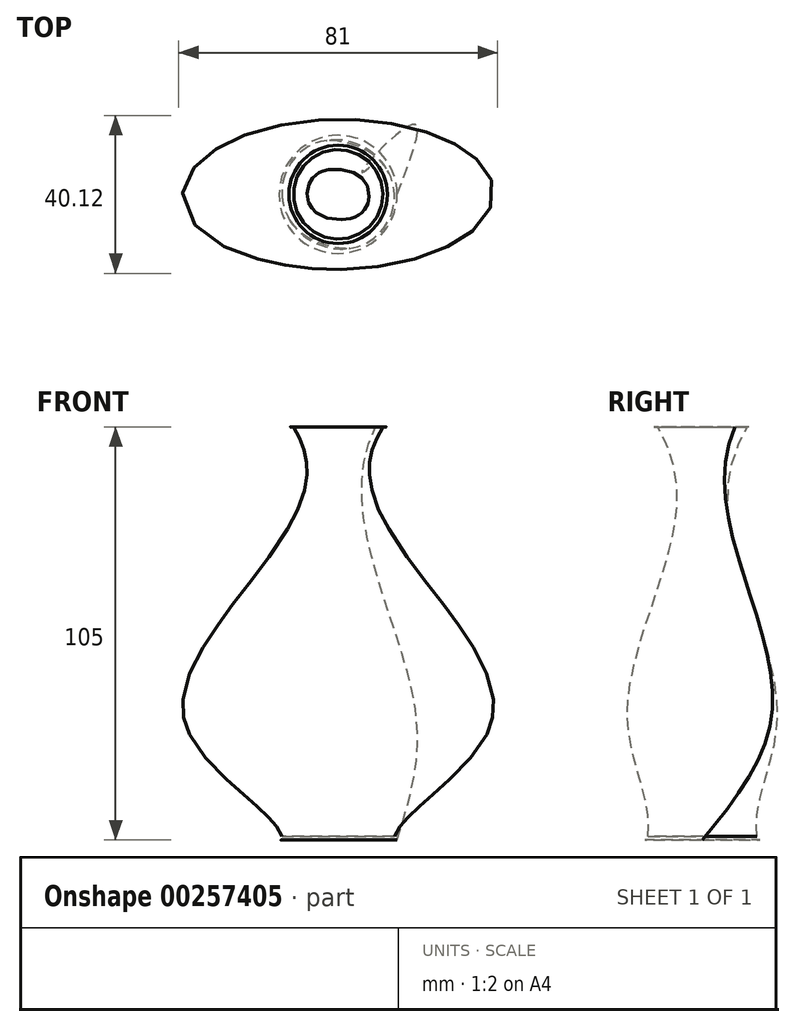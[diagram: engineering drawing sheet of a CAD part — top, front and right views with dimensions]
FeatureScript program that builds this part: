
annotation { "Feature Type Name" : "Feature", "Feature Type Description" : "" }
export const myFeature = defineFeature(function(context is Context, id is Id, definition is map)
    precondition{}
    {
        {
            var Q0;
            Q0=qCreatedBy(makeId("Top.planeOp"),FACE);
            var sketch = newSketch(context, id + "F0", { "sketchPlane" : qUnion([Q0])});
            skCircle(sketch, "E0", {"center": v(0, 0) * mm, "radius": 15 * mm});
            skSolve(sketch);
        }
        {
            var Q0;
            Q0=makeQuery(id+"F0.imprint","IMPRINT",FACE,{"disambiguationData":[TD([[makeQuery(id+"F0.imprint","IMPRINT",EDGE,{"derivedFrom":sQuery(id+"F0.wireOp",EDGE,"E0")}),1.0]])]});
            cPlane(context, id + "F1", {"entities" : qUnion([Q0]), "cplaneType" : CPlaneType.OFFSET, "offset" : 30 * mm, "width" : 150 * mm, "height" : 150 * mm});
        }
        {
            var Q0;
            Q0=qCreatedBy(id+"F1.planeOp",FACE);
            var sketch = newSketch(context, id + "F2", { "sketchPlane" : qUnion([Q0])});
            skEllipse(sketch, "E1", {"center": v(0, 0) * mm, "majorRadius": 40 * mm, "minorRadius": 20 * mm, "majorAxis": v(-1, 0)});
            skSolve(sketch);
        }
        {
            var Q0;
            Q0=makeQuery(id+"F2.imprint","IMPRINT",FACE,{"disambiguationData":[TD([[makeQuery(id+"F2.imprint","IMPRINT",EDGE,{"derivedFrom":sQuery(id+"F2.wireOp",EDGE,"E1")}),1.0]])]});
            cPlane(context, id + "F3", {"entities" : qUnion([Q0]), "cplaneType" : CPlaneType.OFFSET, "offset" : 70 * mm, "width" : 150 * mm, "height" : 150 * mm});
        }
        {
            var Q0;
            Q0=qCreatedBy(id+"F3.planeOp",FACE);
            var sketch = newSketch(context, id + "F4", { "sketchPlane" : qUnion([Q0])});
            skCircle(sketch, "E2", {"center": v(0, 0) * mm, "radius": 10 * mm});
            skSolve(sketch);
        }
        {
            var Q0;
            Q0=makeQuery(id+"F4.imprint","IMPRINT",FACE,{"disambiguationData":[TD([[makeQuery(id+"F4.imprint","IMPRINT",EDGE,{"derivedFrom":sQuery(id+"F4.wireOp",EDGE,"E2")}),1.0]])]});
            cPlane(context, id + "F5", {"entities" : qUnion([Q0]), "cplaneType" : CPlaneType.OFFSET, "offset" : 5 * mm, "width" : 150 * mm, "height" : 150 * mm});
        }
        {
            var Q0;
            Q0=qCreatedBy(id+"F5.planeOp",FACE);
            var sketch = newSketch(context, id + "F6", { "sketchPlane" : qUnion([Q0])});
            skCircle(sketch, "E3", {"center": v(0, 0) * mm, "radius": 12.5 * mm});
            skSolve(sketch);
        }
        {
            var Q0;
            Q0=makeQuery(id+"F0.imprint","IMPRINT",FACE,{"disambiguationData":[TD([[makeQuery(id+"F0.imprint","IMPRINT",EDGE,{"derivedFrom":sQuery(id+"F0.wireOp",EDGE,"E0")}),1.0]])]});
            var Q1;
            Q1=makeQuery(id+"F2.imprint","IMPRINT",FACE,{"disambiguationData":[TD([[makeQuery(id+"F2.imprint","IMPRINT",EDGE,{"derivedFrom":sQuery(id+"F2.wireOp",EDGE,"E1")}),1.0]])]});
            var Q2;
            Q2=makeQuery(id+"F4.imprint","IMPRINT",FACE,{"disambiguationData":[TD([[makeQuery(id+"F4.imprint","IMPRINT",EDGE,{"derivedFrom":sQuery(id+"F4.wireOp",EDGE,"E2")}),1.0]])]});
            var Q3;
            Q3=makeQuery(id+"F6.imprint","IMPRINT",FACE,{"disambiguationData":[TD([[makeQuery(id+"F6.imprint","IMPRINT",EDGE,{"derivedFrom":sQuery(id+"F6.wireOp",EDGE,"E3")}),1.0]])]});
            loft(context, id + "F7", {"sheetProfilesArray" : [{ "sheetProfileEntities" : qUnion([Q0]) }, { "sheetProfileEntities" : qUnion([Q1]) }, { "sheetProfileEntities" : qUnion([Q2]) }, { "sheetProfileEntities" : qUnion([Q3]) }]});
        }
        {
            var Q0;
            Q0=makeQuery(id+"F7.opLoft","CAP_FACE",FACE,{"disambiguationData":[OSD([makeQuery(id+"F6.imprint","IMPRINT",FACE,{"disambiguationData":[TD([[makeQuery(id+"F6.imprint","IMPRINT",EDGE,{"derivedFrom":sQuery(id+"F6.wireOp",EDGE,"E3")}),1.0]])]})])],"isStart":true});
            shell(context, id + "F8", {"entities" : qUnion([Q0]), "thickness" : 1 * mm});
        }
    });
